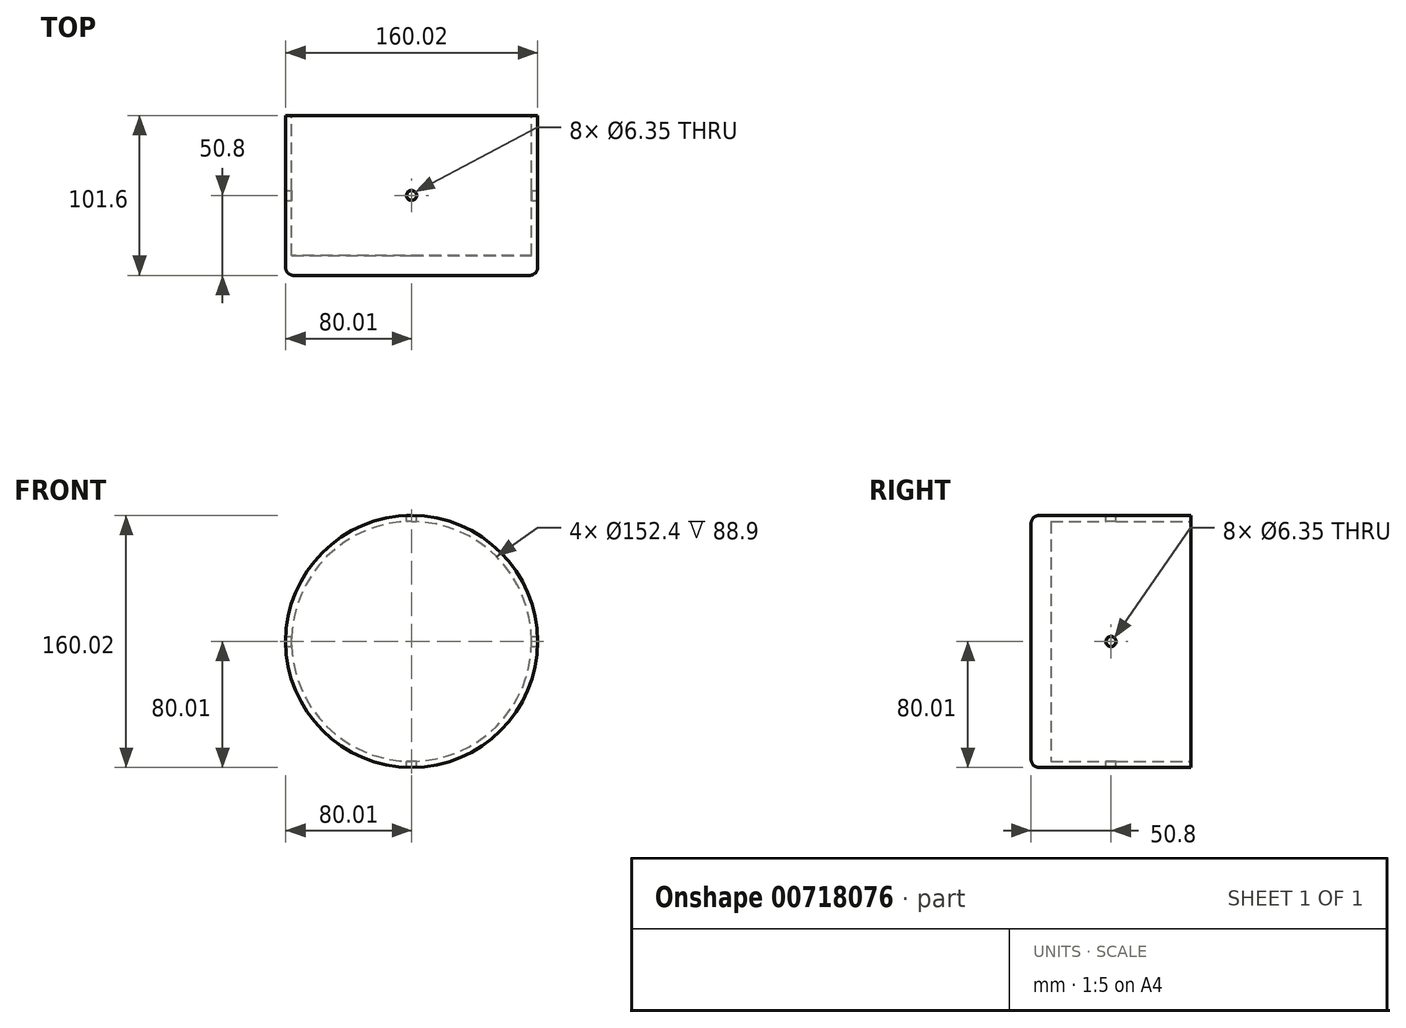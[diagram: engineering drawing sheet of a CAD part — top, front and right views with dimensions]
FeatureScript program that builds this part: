
annotation { "Feature Type Name" : "Feature", "Feature Type Description" : "" }
export const myFeature = defineFeature(function(context is Context, id is Id, definition is map)
    precondition{}
    {
        {
            var Q0;
            Q0=qCreatedBy(makeId("Front.planeOp"),FACE);
            var sketch = newSketch(context, id + "F0", { "sketchPlane" : qUnion([Q0])});
            skCircle(sketch, "E0", {"center": v(0, 0) * mm, "radius": 80.01 * mm});
            skSolve(sketch);
        }
        {
            var Q0;
            Q0 = qSketchRegion(id + "F0", true);
            extrude(context, id + "F1", {"entities" : qUnion([Q0]), "depth" : 101.6 * mm, "offsetDistance" : 25.4 * mm});
        }
        {
            var Q0;
            Q0=makeQuery(id+"F1.opExtrude","CAP_FACE",FACE,{"disambiguationData":[OSD([sQuery(id+"F0.wireOp",EDGE,"E0")])],"isStart":true});
            var sketch = newSketch(context, id + "F2", { "sketchPlane" : qUnion([Q0])});
            skCircle(sketch, "E1", {"center": v(0, 0) * mm, "radius": 76.2 * mm});
            skSolve(sketch);
        }
        {
            var Q0;
            Q0 = qSketchRegion(id + "F2", true);
            extrude(context, id + "F3", {"entities" : qUnion([Q0]), "operationType" : NewBodyOperationType.REMOVE, "oppositeDirection" : true, "depth" : 88.9 * mm, "offsetDistance" : 25.4 * mm});
        }
        {
            var Q0;
            Q0=makeQuery(id+"F1.opExtrude","CAP_EDGE",EDGE,{"disambiguationData":[OSD([sQuery(id+"F0.wireOp",EDGE,"E0")])],"isStart":false});
            fillet(context, id + "F4", {"entities" : qUnion([Q0]), "radius" : 5.08 * mm, "tangentPropagation" : true, "allowEdgeOverflow" : false});
        }
        {
            var Q0;
            Q0=qCreatedBy(makeId("Top.planeOp"),FACE);
            var sketch = newSketch(context, id + "F5", { "sketchPlane" : qUnion([Q0])});
            skLineSegment(sketch, "E2", {"start": v(0, 0) * mm, "end": v(0, 92.38) * mm, "construction": true});
            skLineSegment(sketch, "E3", {"start": v(0, 0) * mm, "end": v(0, -101.6) * mm, "construction": true});
            skCircle(sketch, "E4", {"center": v(0, -50.8) * mm, "radius": 3.17 * mm});
            skSolve(sketch);
        }
        {
            var Q0;
            Q0 = qSketchRegion(id + "F5", true);
            extrude(context, id + "F6", {"entities" : qUnion([Q0]), "operationType" : NewBodyOperationType.REMOVE, "endBound" : BoundingType.SYMMETRIC, "oppositeDirection" : true, "depth" : 254 * mm, "offsetDistance" : 25.4 * mm});
        }
        {
            var Q0;
            Q0=qCreatedBy(makeId("Right.planeOp"),FACE);
            var sketch = newSketch(context, id + "F7", { "sketchPlane" : qUnion([Q0])});
            skLineSegment(sketch, "E5", {"start": v(0, 0) * mm, "end": v(-101.6, 0) * mm, "construction": true});
            skCircle(sketch, "E6", {"center": v(-50.8, 0) * mm, "radius": 3.17 * mm});
            skSolve(sketch);
        }
        {
            var Q0;
            Q0 = qSketchRegion(id + "F7", true);
            extrude(context, id + "F8", {"entities" : qUnion([Q0]), "operationType" : NewBodyOperationType.REMOVE, "endBound" : BoundingType.SYMMETRIC, "oppositeDirection" : true, "depth" : 254 * mm, "offsetDistance" : 25.4 * mm});
        }
    });
